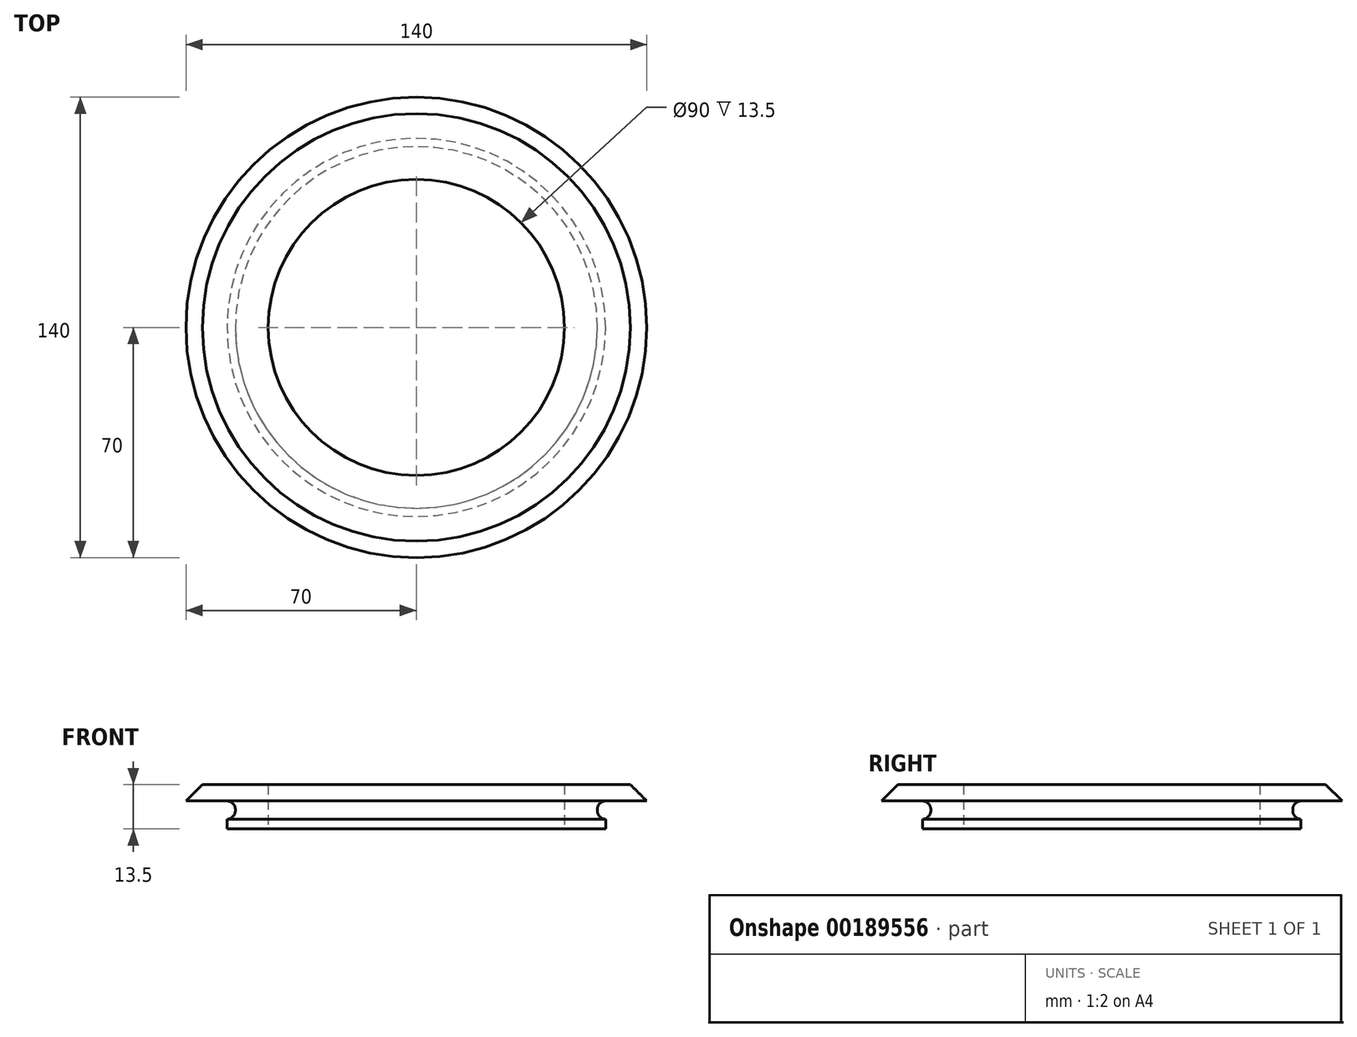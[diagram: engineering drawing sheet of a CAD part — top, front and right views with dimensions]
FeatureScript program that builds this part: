
annotation { "Feature Type Name" : "Feature", "Feature Type Description" : "" }
export const myFeature = defineFeature(function(context is Context, id is Id, definition is map)
    precondition{}
    {
        {
            var Q0;
            Q0=qCreatedBy(makeId("Top.planeOp"),FACE);
            var sketch = newSketch(context, id + "F0", { "sketchPlane" : qUnion([Q0])});
            skCircle(sketch, "E0", {"center": v(0, 0) * mm, "radius": 55 * mm});
            skSolve(sketch);
        }
        {
            var Q0;
            Q0=makeQuery(id+"F0.imprint","IMPRINT",FACE,{"disambiguationData":[TD([[makeQuery(id+"F0.imprint","IMPRINT",EDGE,{"derivedFrom":sQuery(id+"F0.wireOp",EDGE,"E0")}),1.0]])]});
            extrude(context, id + "F1", {"entities" : qUnion([Q0]), "depth" : 5.5 * mm});
        }
        {
            var Q0;
            Q0=makeQuery(id+"F1.opExtrude","CAP_FACE",FACE,{"disambiguationData":[OSD([sQuery(id+"F0.wireOp",EDGE,"E0")])],"isStart":false});
            var sketch = newSketch(context, id + "F2", { "sketchPlane" : qUnion([Q0])});
            skCircle(sketch, "E1", {"center": v(0, 0) * mm, "radius": 70 * mm});
            skSolve(sketch);
        }
        {
            var Q0;
            Q0=makeQuery(id+"F2.imprint","IMPRINT",FACE,{"disambiguationData":[TD([[makeQuery(id+"F2.imprint","IMPRINT",EDGE,{"derivedFrom":sQuery(id+"F2.wireOp",EDGE,"E1")}),1.0]])]});
            var Q1;
            Q1=makeQuery(id+"F2.imprint","IMPRINT",FACE,{"disambiguationData":[TD([[makeQuery(id+"F2.imprint","IMPRINT",EDGE,{"derivedFrom":makeQuery(id+"F1.opExtrude","CAP_EDGE",EDGE,{"disambiguationData":[OSD([sQuery(id+"F0.wireOp",EDGE,"E0")])],"isStart":false})}),1.0]])]});
            extrude(context, id + "F3", {"entities" : qUnion([Q0, Q1]), "operationType" : NewBodyOperationType.ADD, "depth" : 5 * mm});
        }
        {
            var Q0;
            Q0=makeQuery(id+"F3.opExtrude","CAP_EDGE",EDGE,{"disambiguationData":[OSD([sQuery(id+"F2.wireOp",EDGE,"E1")])],"isStart":false});
            chamfer(context, id + "F4", {"entities" : qUnion([Q0]), "width" : 5 * mm, "tangentPropagation" : true});
        }
        {
            var Q0;
            Q0=makeQuery(id+"F1.opExtrude","CAP_FACE",FACE,{"disambiguationData":[OSD([sQuery(id+"F0.wireOp",EDGE,"E0")])],"isStart":true});
            var sketch = newSketch(context, id + "F5", { "sketchPlane" : qUnion([Q0])});
            skCircle(sketch, "E2", {"center": v(0, 0) * mm, "radius": 57.5 * mm});
            skSolve(sketch);
        }
        {
            var Q0;
            Q0=makeQuery(id+"F5.imprint","IMPRINT",FACE,{"disambiguationData":[TD([[makeQuery(id+"F5.imprint","IMPRINT",EDGE,{"derivedFrom":makeQuery(id+"F1.opExtrude","CAP_EDGE",EDGE,{"disambiguationData":[OSD([sQuery(id+"F0.wireOp",EDGE,"E0")])],"isStart":true})}),-1.0]])]});
            var Q1;
            Q1=makeQuery(id+"F5.imprint","IMPRINT",FACE,{"disambiguationData":[TD([[makeQuery(id+"F5.imprint","IMPRINT",EDGE,{"derivedFrom":sQuery(id+"F5.wireOp",EDGE,"E2")}),1.0]])]});
            extrude(context, id + "F6", {"entities" : qUnion([Q0, Q1]), "operationType" : NewBodyOperationType.ADD, "depth" : 3 * mm});
        }
        {
            var Q0;
            Q0=makeQuery(id+"F1.opExtrude","CAP_EDGE",EDGE,{"disambiguationData":[OSD([sQuery(id+"F0.wireOp",EDGE,"E0")])],"isStart":false});
            var Q1;
            Q1=makeQuery(id+"F1.opExtrude","SWEPT_FACE",FACE,{"disambiguationData":[OSD([sQuery(id+"F0.wireOp",EDGE,"E0")])]});
            fillet(context, id + "F7", {"entities" : qUnion([Q0, Q1]), "radius" : 2.5 * mm, "tangentPropagation" : true, "allowEdgeOverflow" : false});
        }
        {
            var Q0;
            Q0=makeQuery(id+"F6.opExtrude","CAP_FACE",FACE,{"disambiguationData":[OSD([sQuery(id+"F5.wireOp",EDGE,"E2")])],"isStart":false});
            var sketch = newSketch(context, id + "F8", { "sketchPlane" : qUnion([Q0])});
            skPoint(sketch, "E3", {"position": v(0, 0) * mm});
            skSolve(sketch);
        }
        {
            var Q0;
            Q0=sQuery(id+"F8.wireOp",VERTEX,"E3");
            var Q1;
            Q1=makeQuery(id+"F1.opExtrude","SWEPT_BODY",BODY,{"disambiguationData":[OSD([sQuery(id+"F0.wireOp",EDGE,"E0")])]});
            hole(context, id + "F9", {"style" : HoleStyle.SIMPLE, "endStyle" : HoleEndStyle.BLIND, "holeDiameter" : 90 * mm, "holeDepth" : 68 * mm, "locations" : qUnion([Q0]), "scope" : qUnion([Q1])});
        }
    });
